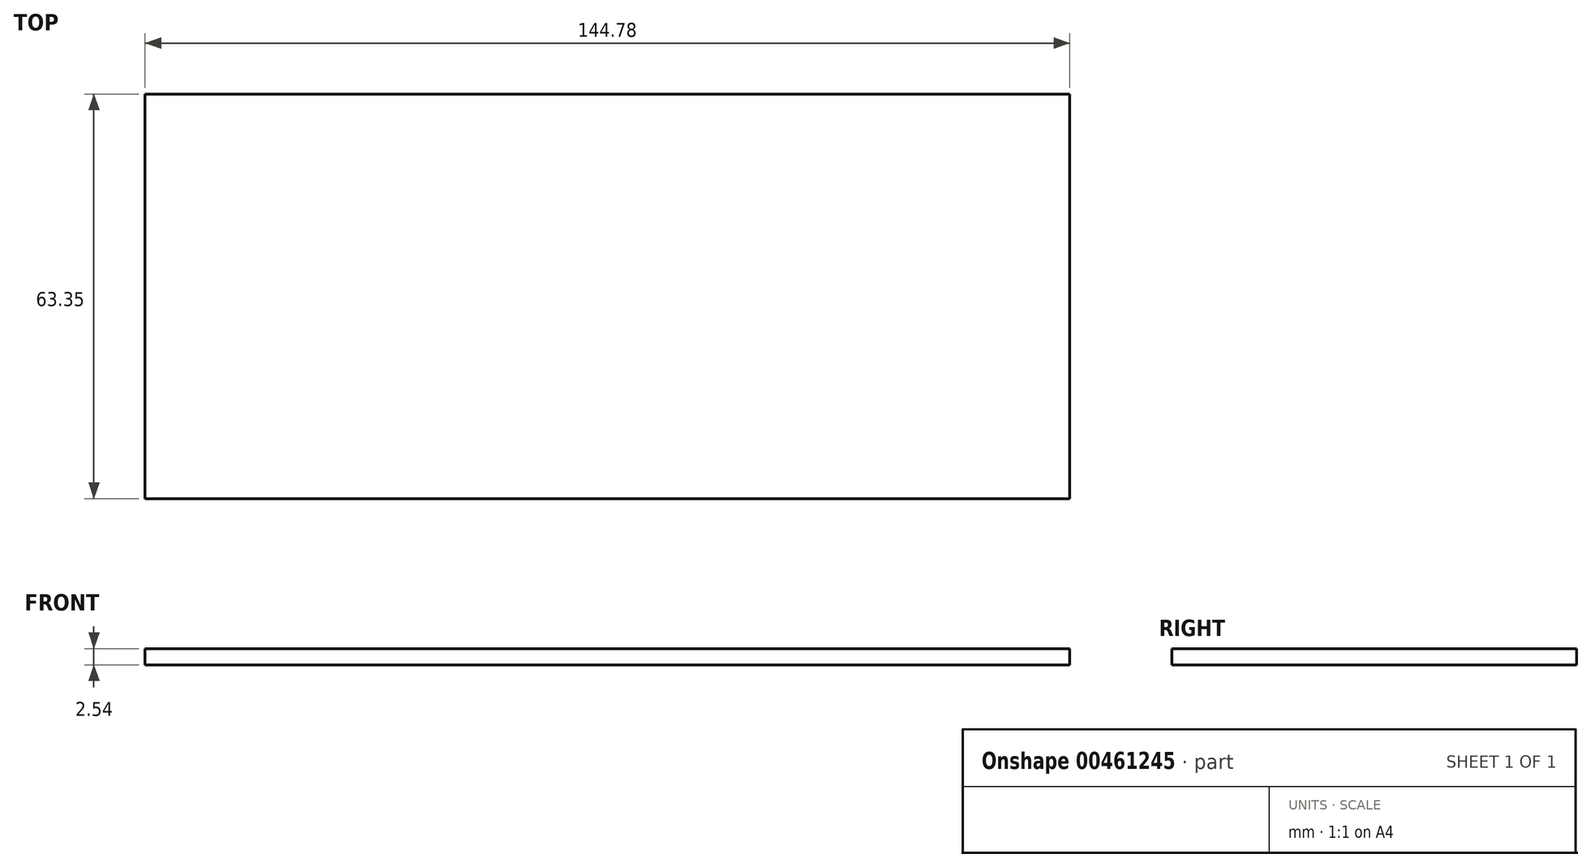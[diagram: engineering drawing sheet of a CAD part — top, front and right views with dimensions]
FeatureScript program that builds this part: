
annotation { "Feature Type Name" : "Feature", "Feature Type Description" : "" }
export const myFeature = defineFeature(function(context is Context, id is Id, definition is map)
    precondition{}
    {
        {
            var Q0;
            Q0=qCreatedBy(makeId("Top.planeOp"),FACE);
            var sketch = newSketch(context, id + "F0", { "sketchPlane" : qUnion([Q0])});
            skLineSegment(sketch, "E0.bottom", {"start": v(-73.9, 43.39) * mm, "end": v(70.88, 43.39) * mm});
            skLineSegment(sketch, "E0.top", {"start": v(-73.9, -19.96) * mm, "end": v(70.88, -19.96) * mm});
            skLineSegment(sketch, "E0.left", {"start": v(-73.9, 43.39) * mm, "end": v(-73.9, -19.96) * mm});
            skLineSegment(sketch, "E0.right", {"start": v(70.88, 43.39) * mm, "end": v(70.88, -19.96) * mm});
            skSolve(sketch);
        }
        {
            var Q0;
            Q0=qSketchRegion(id+"F0",true);
            extrude(context, id + "F1", {"entities" : qUnion([Q0]), "depth" : 2.54 * mm});
        }
    });
